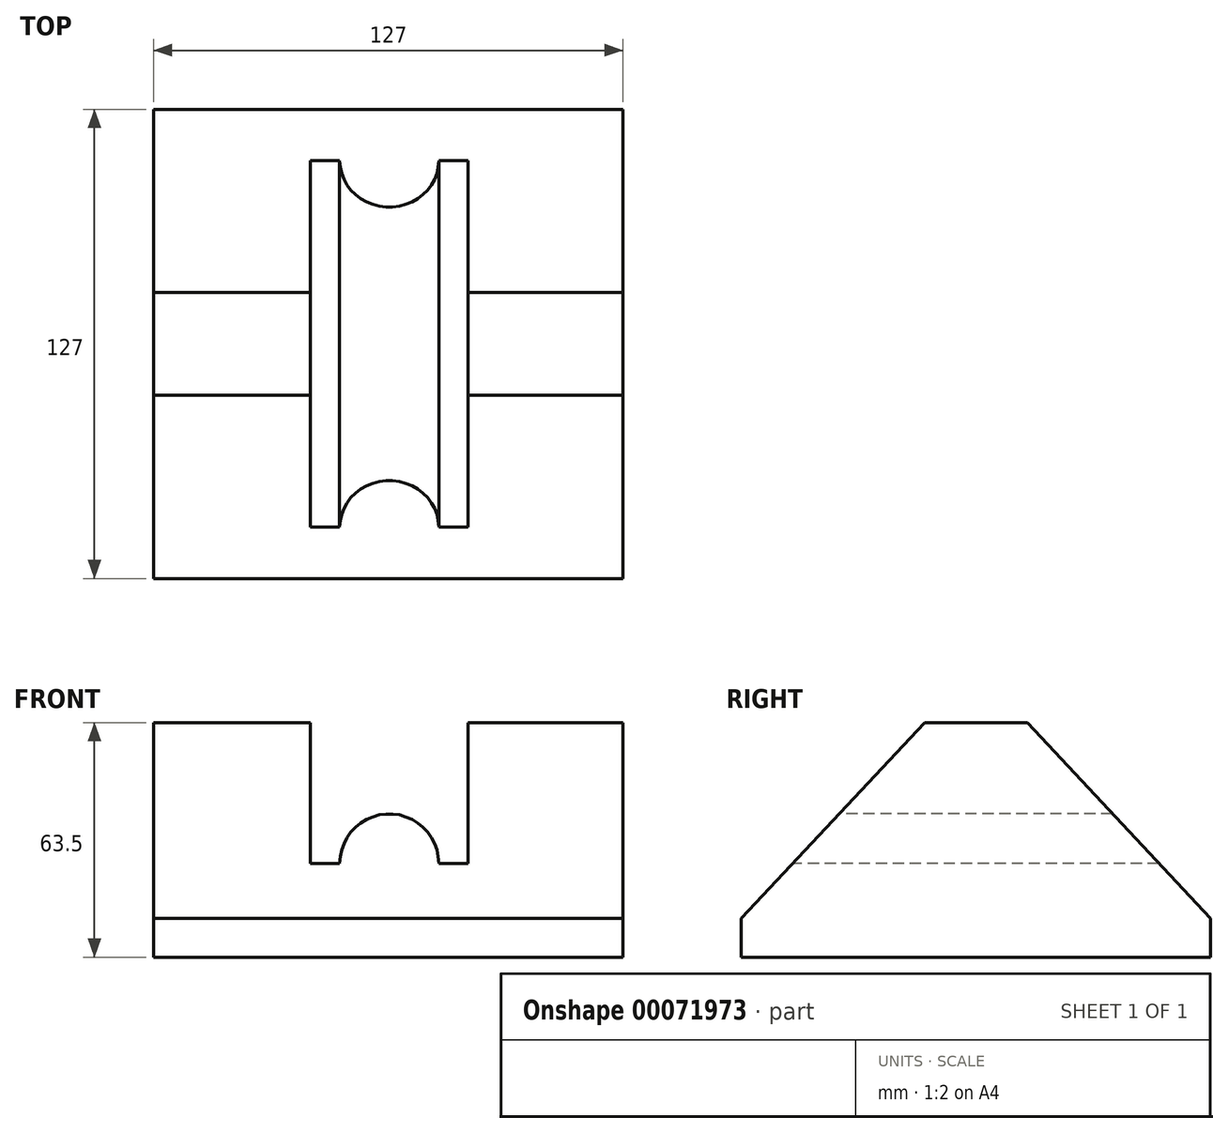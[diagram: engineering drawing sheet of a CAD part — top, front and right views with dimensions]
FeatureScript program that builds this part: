
annotation { "Feature Type Name" : "Feature", "Feature Type Description" : "" }
export const myFeature = defineFeature(function(context is Context, id is Id, definition is map)
    precondition{}
    {
        {
            var Q0;
            Q0=qCreatedBy(makeId("Top.planeOp"),FACE);
            var sketch = newSketch(context, id + "F0", { "sketchPlane" : qUnion([Q0])});
            skLineSegment(sketch, "E0", {"start": v(0, 63.5) * mm, "end": v(63.5, 63.5) * mm});
            skLineSegment(sketch, "E1", {"start": v(63.5, 63.5) * mm, "end": v(63.5, 0) * mm});
            skLineSegment(sketch, "E2.MirrorCS", {"start": v(-63.5, 63.5) * mm, "end": v(-63.5, 0) * mm});
            skLineSegment(sketch, "E3.MirrorCS", {"start": v(0, 63.5) * mm, "end": v(-63.5, 63.5) * mm});
            skLineSegment(sketch, "E4.MirrorCS", {"start": v(0, -63.5) * mm, "end": v(-63.5, -63.5) * mm});
            skLineSegment(sketch, "E5.MirrorCS", {"start": v(-63.5, -63.5) * mm, "end": v(-63.5, 0) * mm});
            skLineSegment(sketch, "E6.MirrorCS", {"start": v(0, -63.5) * mm, "end": v(63.5, -63.5) * mm});
            skLineSegment(sketch, "E7.MirrorCS", {"start": v(63.5, -63.5) * mm, "end": v(63.5, 0) * mm});
            skSolve(sketch);
        }
        {
            var Q0;
            Q0=makeQuery(id+"F0.imprint","IMPRINT",FACE,{"disambiguationData":[TD([[makeQuery(id+"F0.imprint","IMPRINT",EDGE,{"derivedFrom":sQuery(id+"F0.wireOp",EDGE,"E0")}),-1.0]])]});
            extrude(context, id + "F1", {"entities" : qUnion([Q0]), "depth" : 25.4 * mm});
        }
        {
            var Q0;
            Q0=makeQuery(id+"F1.opExtrude","CAP_FACE",FACE,{"disambiguationData":[OSD([sQuery(id+"F0.wireOp",EDGE,"E0"),sQuery(id+"F0.wireOp",EDGE,"E1"),sQuery(id+"F0.wireOp",EDGE,"E2.MirrorCS"),sQuery(id+"F0.wireOp",EDGE,"E3.MirrorCS"),sQuery(id+"F0.wireOp",EDGE,"E4.MirrorCS"),sQuery(id+"F0.wireOp",EDGE,"E5.MirrorCS"),sQuery(id+"F0.wireOp",EDGE,"E6.MirrorCS"),sQuery(id+"F0.wireOp",EDGE,"E7.MirrorCS")])],"isStart":false});
            var sketch = newSketch(context, id + "F2", { "sketchPlane" : qUnion([Q0])});
            skLineSegment(sketch, "E8", {"start": v(21.58, 63.5) * mm, "end": v(21.58, -63.5) * mm});
            skSolve(sketch);
        }
        {
            var Q0;
            Q0=makeQuery(id+"F1.opExtrude","CAP_FACE",FACE,{"disambiguationData":[OSD([sQuery(id+"F0.wireOp",EDGE,"E0"),sQuery(id+"F0.wireOp",EDGE,"E1"),sQuery(id+"F0.wireOp",EDGE,"E2.MirrorCS"),sQuery(id+"F0.wireOp",EDGE,"E3.MirrorCS"),sQuery(id+"F0.wireOp",EDGE,"E4.MirrorCS"),sQuery(id+"F0.wireOp",EDGE,"E5.MirrorCS"),sQuery(id+"F0.wireOp",EDGE,"E6.MirrorCS"),sQuery(id+"F0.wireOp",EDGE,"E7.MirrorCS")])],"isStart":false});
            var sketch = newSketch(context, id + "F3", { "sketchPlane" : qUnion([Q0])});
            skLineSegment(sketch, "E9", {"start": v(-21.02, 63.5) * mm, "end": v(-21.02, -63.5) * mm});
            skSolve(sketch);
        }
        {
            var Q0;
            {var subQ0=sQuery(id+"F3.wireOp",EDGE,"E9");Q0=makeQuery(id+"F3.imprint","IMPRINT",FACE,{"disambiguationData":[TD([[makeQuery(id+"F3.imprint","IMPRINT",EDGE,{"derivedFrom":subQ0}),-1.0]])]});}
            extrude(context, id + "F4", {"entities" : qUnion([Q0]), "operationType" : NewBodyOperationType.ADD, "depth" : 38.1 * mm});
        }
        {
            var Q0;
            {var subQ0=sQuery(id+"F2.wireOp",EDGE,"E8");Q0=makeQuery(id+"F2.imprint","IMPRINT",FACE,{"disambiguationData":[TD([[makeQuery(id+"F2.imprint","IMPRINT",EDGE,{"derivedFrom":subQ0}),1.0]])]});}
            extrude(context, id + "F5", {"entities" : qUnion([Q0]), "operationType" : NewBodyOperationType.ADD, "depth" : 38.1 * mm});
        }
        {
            var Q0;
            {var subQ0=sQuery(id+"F0.wireOp",EDGE,"E6.MirrorCS");var subQ1=sQuery(id+"F0.wireOp",EDGE,"E4.MirrorCS");Q0=makeQuery(id+"F5.boolean.opBoolean","MERGE",FACE,{"derivedFrom":[makeQuery(id+"F4.boolean.opBoolean","MERGE",FACE,{"derivedFrom":[makeQuery(id+"F1.opExtrude","SWEPT_FACE",FACE,{"disambiguationData":[OSD([subQ1,subQ0])]}),makeQuery(id+"F4.opExtrude","SWEPT_FACE",FACE,{"disambiguationData":[OSD([subQ1,subQ0])]})]}),makeQuery(id+"F5.opExtrude","SWEPT_FACE",FACE,{"disambiguationData":[OSD([subQ1,subQ0])]})]});}
            var sketch = newSketch(context, id + "F6", { "sketchPlane" : qUnion([Q0])});
            skArc(sketch, "E10", {"start": v(13.72, 25.4) * mm, "mid": v(0.28, 38.84) * mm, "end": v(-13.16, 25.4) * mm});
            skLineSegment(sketch, "E11", {"start": v(-13.16, 25.4) * mm, "end": v(13.72, 25.4) * mm});
            skSolve(sketch);
        }
        {
            var Q0;
            Q0=makeQuery(id+"F6.imprint","IMPRINT",FACE,{"disambiguationData":[TD([[makeQuery(id+"F6.imprint","IMPRINT",EDGE,{"derivedFrom":sQuery(id+"F6.wireOp",EDGE,"E10")}),1.0]])]});
            extrude(context, id + "F7", {"entities" : qUnion([Q0]), "operationType" : NewBodyOperationType.ADD, "oppositeDirection" : true, "depth" : 127 * mm});
        }
        {
            var Q0;
            {var subQ0=sQuery(id+"F0.wireOp",EDGE,"E7.MirrorCS");var subQ1=sQuery(id+"F0.wireOp",EDGE,"E1");Q0=makeQuery(id+"F5.boolean.opBoolean","MERGE",FACE,{"derivedFrom":[makeQuery(id+"F1.opExtrude","SWEPT_FACE",FACE,{"disambiguationData":[OSD([subQ1,subQ0])]}),makeQuery(id+"F5.opExtrude","SWEPT_FACE",FACE,{"disambiguationData":[OSD([subQ1,subQ0])]})]});}
            var sketch = newSketch(context, id + "F8", { "sketchPlane" : qUnion([Q0])});
            skLineSegment(sketch, "E12", {"start": v(-13.9, 63.5) * mm, "end": v(-63.5, 10.48) * mm});
            skLineSegment(sketch, "E13", {"start": v(-63.5, 10.48) * mm, "end": v(-63.5, 63.5) * mm});
            skLineSegment(sketch, "E14", {"start": v(-63.5, 63.5) * mm, "end": v(-13.9, 63.5) * mm});
            skLineSegment(sketch, "E15.MirrorCS", {"start": v(63.5, 63.5) * mm, "end": v(13.9, 63.5) * mm});
            skLineSegment(sketch, "E16.MirrorCS", {"start": v(63.5, 10.48) * mm, "end": v(63.5, 63.5) * mm});
            skLineSegment(sketch, "E17.MirrorCS", {"start": v(13.9, 63.5) * mm, "end": v(63.5, 10.48) * mm});
            skSolve(sketch);
        }
        {
            var Q0;
            Q0 = qSketchRegion(id + "F8", true);
            extrude(context, id + "F9", {"entities" : qUnion([Q0]), "operationType" : NewBodyOperationType.REMOVE, "endBound" : BoundingType.THROUGH_ALL, "oppositeDirection" : true, "depth" : 25.4 * mm});
        }
    });
